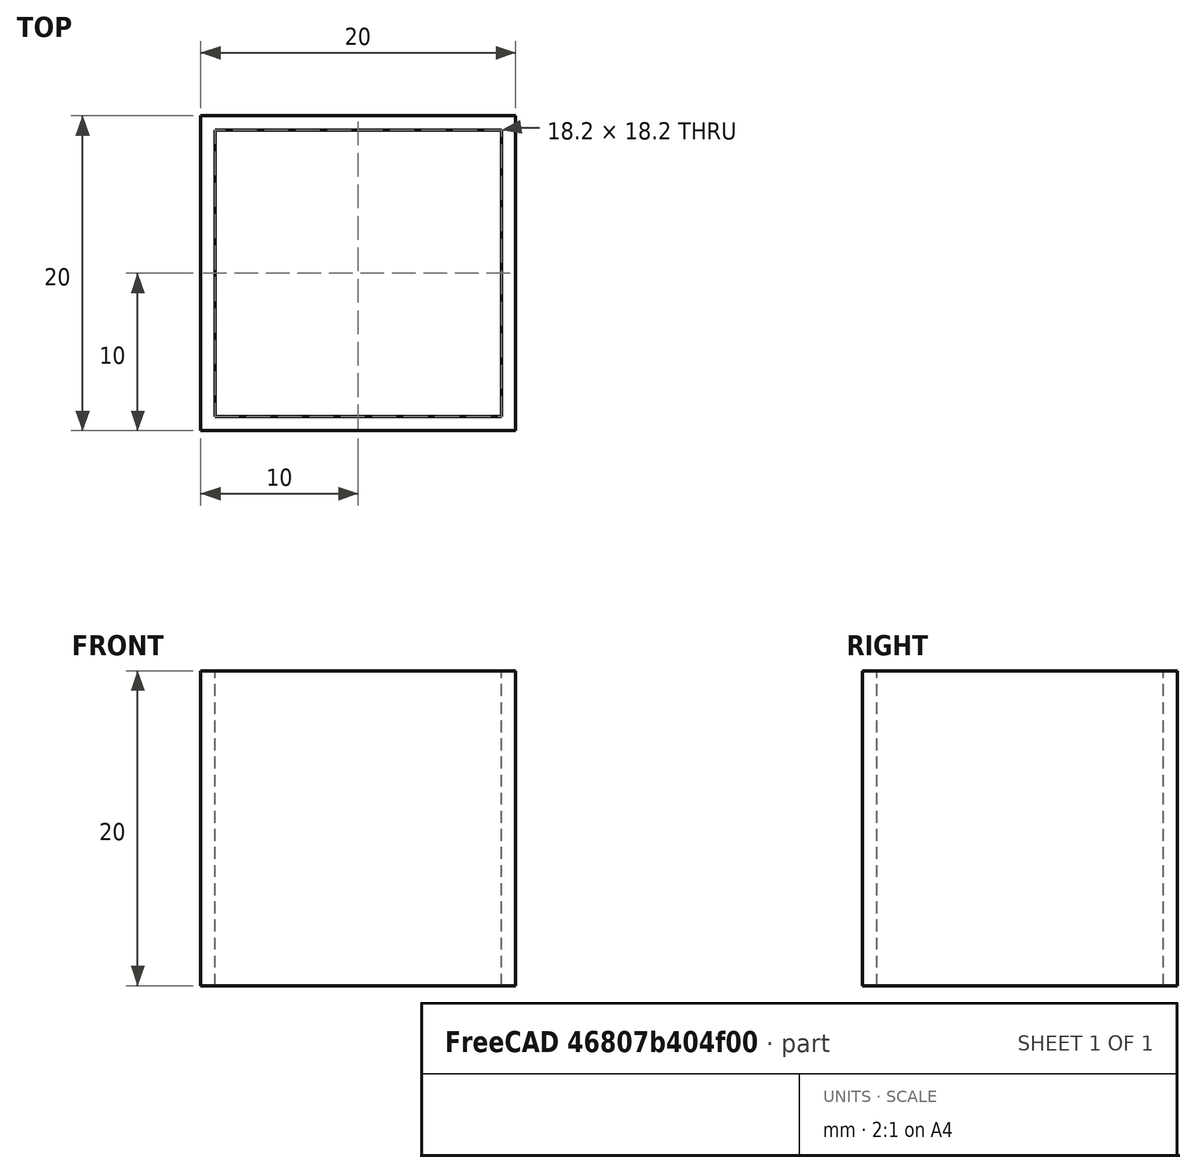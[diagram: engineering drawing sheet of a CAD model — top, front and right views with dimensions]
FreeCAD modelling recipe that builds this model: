
FCSTD DOCUMENT  (FreeCAD 0.21R38947 (Git))
Label: wall-width-test-0_9mm
License: All rights reserved
LicenseURL: https://en.wikipedia.org/wiki/All_rights_reserved
objects: Sketcher::SketchObject×1, PartDesign::Pad×1, PartDesign::Body×1
note: 6 computed .brp shape members not serialized (recipe doc carries the construction recipe); baked Part::Feature solids carry a one-line shape summary decoded from their .brp

FEATURE [Sketcher::SketchObject] Sketch
  ArcFitTolerance = 1e-06
  AttachmentSupport = -> [XY_Plane]
  ExternalBSplineMaxDegree = 5
  ExternalBSplineTolerance = 0.0001
  FullyConstrained = true
  InternalTolerance = 1e-06
  InvalidShape = false
  MakeInternals = false
  MapMode = 5
  Support = -> [XY_Plane]
  TreeRank = 13
  ValidateShape = false
  sketch-geometry (12):
    g0: LineSegment StartX=-9.1 StartY=-9.1 StartZ=0 EndX=-9.1 EndY=9.1 EndZ=0
    g1: LineSegment StartX=-9.1 StartY=9.1 StartZ=0 EndX=9.1 EndY=9.1 EndZ=0
    g2: LineSegment StartX=9.1 StartY=9.1 StartZ=0 EndX=9.1 EndY=-9.1 EndZ=0
    g3: LineSegment StartX=9.1 StartY=-9.1 StartZ=0 EndX=-9.1 EndY=-9.1 EndZ=0
    g4: GeomPoint [constr] X=0 Y=0 Z=0
    g5: LineSegment StartX=-10 StartY=-10 StartZ=0 EndX=-10 EndY=10 EndZ=0
    g6: LineSegment StartX=-10 StartY=10 StartZ=0 EndX=10 EndY=10 EndZ=0
    g7: LineSegment StartX=10 StartY=10 StartZ=0 EndX=10 EndY=-10 EndZ=0
    g8: LineSegment StartX=10 StartY=-10 StartZ=0 EndX=-10 EndY=-10 EndZ=0
    g9: GeomPoint [constr] X=0 Y=0 Z=0
    g10: LineSegment [constr] StartX=9.1 StartY=9.1 StartZ=0 EndX=10 EndY=9.1 EndZ=0
    g11: LineSegment [constr] StartX=9.1 StartY=9.1 StartZ=0 EndX=9.1 EndY=10 EndZ=0
  constraints (30):
    c: Coincident(g0,g1)
    c: Coincident(g1,g2)
    c: Coincident(g2,g3)
    c: Coincident(g3,g0)
    c: Horizontal(g1)
    c: Horizontal(g3)
    c: Vertical(g0)
    c: Vertical(g2)
    c: Symmetric(g1,g0,g4)
    c: Coincident(g4,g-1)
    c: Coincident(g5,g6)
    c: Coincident(g6,g7)
    c: Coincident(g7,g8)
    c: Coincident(g8,g5)
    c: Horizontal(g6)
    c: Horizontal(g8)
    c: Vertical(g5)
    c: Vertical(g7)
    c: Symmetric(g6,g5,g9)
    c: Coincident(g9,g4)
    c: Coincident(g10,g1)
    c: PointOnObject(g10,g7)
    c: Horizontal(g10)
    c: Coincident(g11,g1)
    c: PointOnObject(g11,g6)
    c: Vertical(g11)
    c: Equal(g11,g10)
    c: DistanceY(g11,g11) = 0.9
    c: DistanceY(g7,g7) = 20
    c: Equal(g7,g6)
FEATURE [PartDesign::Pad] Pad
  AddSubType = 0
  AlongSketchNormal = false
  AutoTaperInnerAngle = true
  CheckUpToFaceLimits = true
  ClaimChildren = false
  Direction = (0,0,1)
  Fit = 0
  FitJoin = 0
  InnerFit = 0
  InnerFitJoin = 0
  InvalidShape = false
  Length = 20
  Length2 = 10
  Linearize = true
  NewSolid = false
  Profile = -> Sketch
  ReferenceAxis = -> Sketch [N_Axis]
  Suppress = false
  TaperInnerAngle = 0
  TaperInnerAngleRev = 0
  TreeRank = 14
  Type = 0
  ValidateShape = true
  _ProfileBasedVersion = 1
FEATURE [PartDesign::Body] Body  label="wall-width-test-0_9mm"
  AutoGroupSolids = false
  ClaimAllChildren = false
  ExportMode = 0
  Group = -> [Sketch,Pad]
  InvalidShape = false
  Origin = -> Origin
  Tip = -> Pad
  TreeRank = 12
  ValidateShape = false
  _ExportChildren = -> [Pad]
  _GroupVersion = 1
